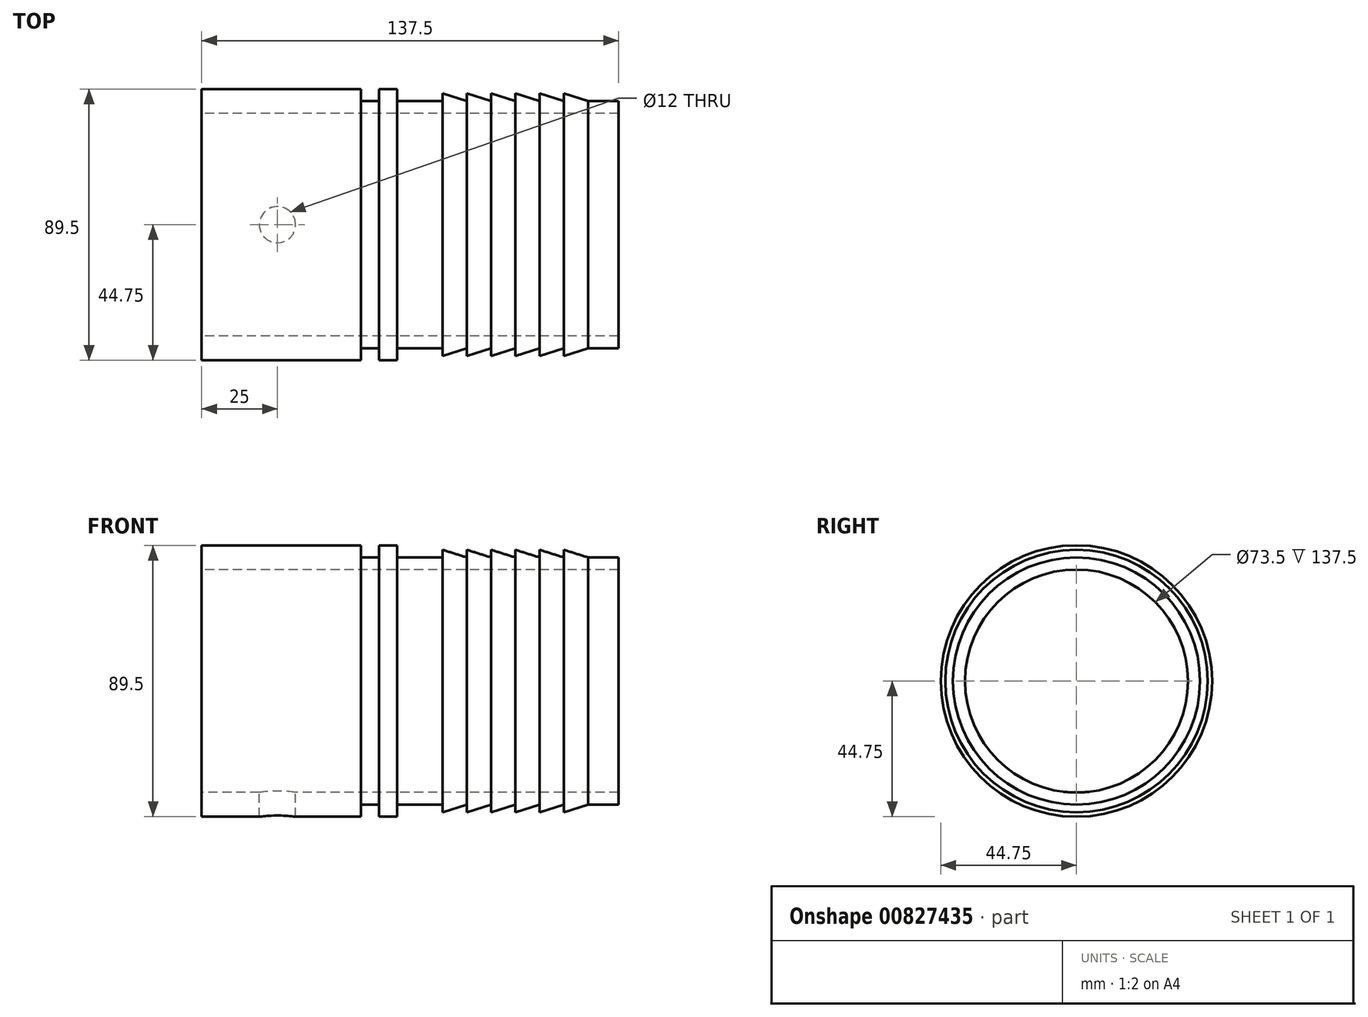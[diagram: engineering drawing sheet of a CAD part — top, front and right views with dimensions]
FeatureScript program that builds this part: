
annotation { "Feature Type Name" : "Feature", "Feature Type Description" : "" }
export const myFeature = defineFeature(function(context is Context, id is Id, definition is map)
    precondition{}
    {
        {
            var Q0;
            Q0=qCreatedBy(makeId("Front.planeOp"),FACE);
            var sketch = newSketch(context, id + "F0", { "sketchPlane" : qUnion([Q0])});
            skLineSegment(sketch, "E0", {"start": v(-86.07, 0) * mm, "end": v(128.54, 0) * mm, "construction": true});
            skLineSegment(sketch, "E1", {"start": v(0, 36.75) * mm, "end": v(0, 44.75) * mm});
            skLineSegment(sketch, "E2", {"start": v(52.5, 40.75) * mm, "end": v(58.5, 40.75) * mm});
            skLineSegment(sketch, "E3", {"start": v(58.5, 40.75) * mm, "end": v(58.5, 44.75) * mm});
            skLineSegment(sketch, "E4", {"start": v(58.5, 44.75) * mm, "end": v(64.5, 44.75) * mm});
            skLineSegment(sketch, "E5", {"start": v(64.5, 44.75) * mm, "end": v(64.5, 40.75) * mm});
            skLineSegment(sketch, "E6", {"start": v(64.5, 40.75) * mm, "end": v(79.5, 40.75) * mm});
            skLineSegment(sketch, "E7", {"start": v(79.5, 40.75) * mm, "end": v(79.5, 43.25) * mm});
            skLineSegment(sketch, "E8", {"start": v(79.5, 43.25) * mm, "end": v(87.5, 40.75) * mm});
            skLineSegment(sketch, "E9", {"start": v(87.5, 40.75) * mm, "end": v(87.5, 43.25) * mm});
            skLineSegment(sketch, "E10", {"start": v(87.5, 43.25) * mm, "end": v(95.5, 40.75) * mm});
            skLineSegment(sketch, "E11", {"start": v(95.5, 40.75) * mm, "end": v(95.5, 43.25) * mm});
            skLineSegment(sketch, "E12", {"start": v(95.5, 43.25) * mm, "end": v(103.5, 40.75) * mm});
            skLineSegment(sketch, "E13", {"start": v(103.5, 40.75) * mm, "end": v(103.5, 43.25) * mm});
            skLineSegment(sketch, "E14", {"start": v(103.5, 43.25) * mm, "end": v(111.5, 40.75) * mm});
            skLineSegment(sketch, "E15", {"start": v(111.5, 40.75) * mm, "end": v(111.5, 43.25) * mm});
            skLineSegment(sketch, "E16", {"start": v(111.5, 43.25) * mm, "end": v(119.5, 40.75) * mm});
            skLineSegment(sketch, "E17", {"start": v(119.5, 40.75) * mm, "end": v(119.5, 43.25) * mm});
            skLineSegment(sketch, "E18", {"start": v(119.5, 43.25) * mm, "end": v(127.5, 40.75) * mm});
            skLineSegment(sketch, "E19", {"start": v(127.5, 40.75) * mm, "end": v(137.5, 40.75) * mm});
            skLineSegment(sketch, "E20", {"start": v(137.5, 40.75) * mm, "end": v(137.5, 36.75) * mm});
            skLineSegment(sketch, "E21", {"start": v(137.5, 36.75) * mm, "end": v(0, 36.75) * mm});
            skLineSegment(sketch, "E22", {"start": v(52.5, 40.75) * mm, "end": v(52.5, 44.75) * mm});
            skLineSegment(sketch, "E23", {"start": v(52.5, 44.75) * mm, "end": v(0, 44.75) * mm});
            skSolve(sketch);
        }
        {
            var Q0;
            Q0=makeQuery(id+"F0.imprint","IMPRINT",FACE,{"disambiguationData":[TD([[makeQuery(id+"F0.imprint","IMPRINT",EDGE,{"derivedFrom":sQuery(id+"F0.wireOp",EDGE,"E1")}),-1.0]])]});
            var Q1;
            Q1=sQuery(id+"F0.wireOp",EDGE,"E0");
            revolve(context, id + "F1", {"surfaceOperationType" : NewSurfaceOperationType.NEW, "entities" : qUnion([Q0]), "axis" : qUnion([Q1]), "revolveType" : RevolveType.FULL});
        }
        {
            var Q0;
            Q0=qCreatedBy(makeId("Top.planeOp"),FACE);
            var sketch = newSketch(context, id + "F2", { "sketchPlane" : qUnion([Q0])});
            skCircle(sketch, "E24", {"center": v(25, 0) * mm, "radius": 6 * mm});
            skSolve(sketch);
        }
        {
            var Q0;
            Q0=makeQuery(id+"F2.imprint","IMPRINT",FACE,{"disambiguationData":[TD([[makeQuery(id+"F2.imprint","IMPRINT",EDGE,{"derivedFrom":sQuery(id+"F2.wireOp",EDGE,"E24")}),1.0]])]});
            extrude(context, id + "F3", {"entities" : qUnion([Q0]), "operationType" : NewBodyOperationType.REMOVE, "oppositeDirection" : true, "depth" : 100 * mm, "offsetDistance" : 25 * mm});
        }
    });
